# Revit family: TMR1_63_UN_Emergency Lighting_Surface-mounted_Recessed_ETK
name_source: partatom
category: Lighting Fixtures
units: mm (PartAtom-declared; Revit-internal decimal feet)

## family parameters
Always vertical = Yes
Cut with Voids When Loaded = No
Light Source = No
OmniClass Number = 23.80.70.11.14.11
OmniClass Title = Downlights
Part Type = Normal
Room Calculation Point = Yes
Round Connector Dimension = Use Diameter
Shared = No
Work Plane-Based = No

## types (2) — shared parameters
Apparent Load = 2 VA
Assembly Code = 63.0
Description = Surface Mounted and Recessed
IfcExportAs = IfcLightFixtureType
IfcExportType = USERDEFINED
Lamp = LED
Light Source = TMR.1 - Lightsource : TMR.1100.xxN - 2W / 360lm / 1hr autonomy
Luminaire_Body_Material = PPS Plastic
Manufacturer = ETK licht B.V.
Model = TMR1
Type Comments = IP66 - IK10
URL = https://www.etk.nl
Voltage = 230 V
Wattage Comments = 2W

## type names (no varying parameters)
- TMR.1100.xxN - 2W / 360lm / 1hr autonomy
- TMR.1200.xxN - 2W / 360lm / 1hr autonomy

## geometry (parser evidence)
native form markers: Sweep x5
no freeform markers — native parametric forms only
